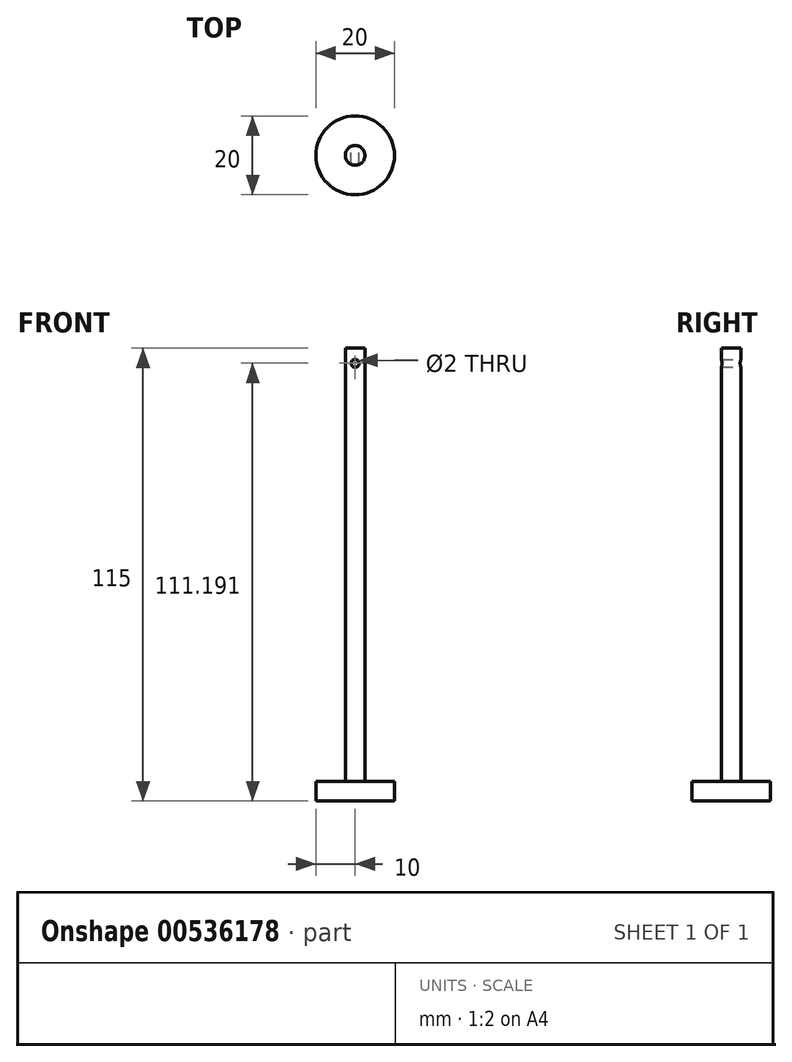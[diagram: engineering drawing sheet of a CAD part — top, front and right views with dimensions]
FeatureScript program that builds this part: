
annotation { "Feature Type Name" : "Feature", "Feature Type Description" : "" }
export const myFeature = defineFeature(function(context is Context, id is Id, definition is map)
    precondition{}
    {
        {
            var Q0;
            Q0=qCreatedBy(makeId("Top.planeOp"),FACE);
            var sketch = newSketch(context, id + "F0", { "sketchPlane" : qUnion([Q0])});
            skCircle(sketch, "E0", {"center": v(0, 0) * mm, "radius": 10 * mm});
            skCircle(sketch, "E1", {"center": v(0, 0) * mm, "radius": 2.5 * mm});
            skSolve(sketch);
        }
        {
            var Q0;
            Q0=makeQuery(id+"F0.imprint","IMPRINT",FACE,{"disambiguationData":[TD([[makeQuery(id+"F0.imprint","IMPRINT",EDGE,{"derivedFrom":sQuery(id+"F0.wireOp",EDGE,"E1")}),1.0]])]});
            extrude(context, id + "F1", {"entities" : qUnion([Q0]), "depth" : 115 * mm, "offsetDistance" : 25 * mm});
        }
        {
            var Q0;
            Q0 = qSketchRegion(id + "F0", true);
            extrude(context, id + "F2", {"entities" : qUnion([Q0]), "operationType" : NewBodyOperationType.ADD, "depth" : 5 * mm, "offsetDistance" : 25 * mm});
        }
        {
            var Q0;
            Q0=qCreatedBy(makeId("Front.planeOp"),FACE);
            var sketch = newSketch(context, id + "F3", { "sketchPlane" : qUnion([Q0])});
            skPoint(sketch, "E2", {"position": v(0, 111.2) * mm});
            skCircle(sketch, "E3", {"center": v(0, 111.2) * mm, "radius": 1 * mm});
            skSolve(sketch);
        }
        {
            var Q0;
            Q0 = qSketchRegion(id + "F3", true);
            extrude(context, id + "F4", {"entities" : qUnion([Q0]), "operationType" : NewBodyOperationType.REMOVE, "endBound" : BoundingType.SYMMETRIC, "depth" : 10 * mm, "offsetDistance" : 25 * mm});
        }
    });
